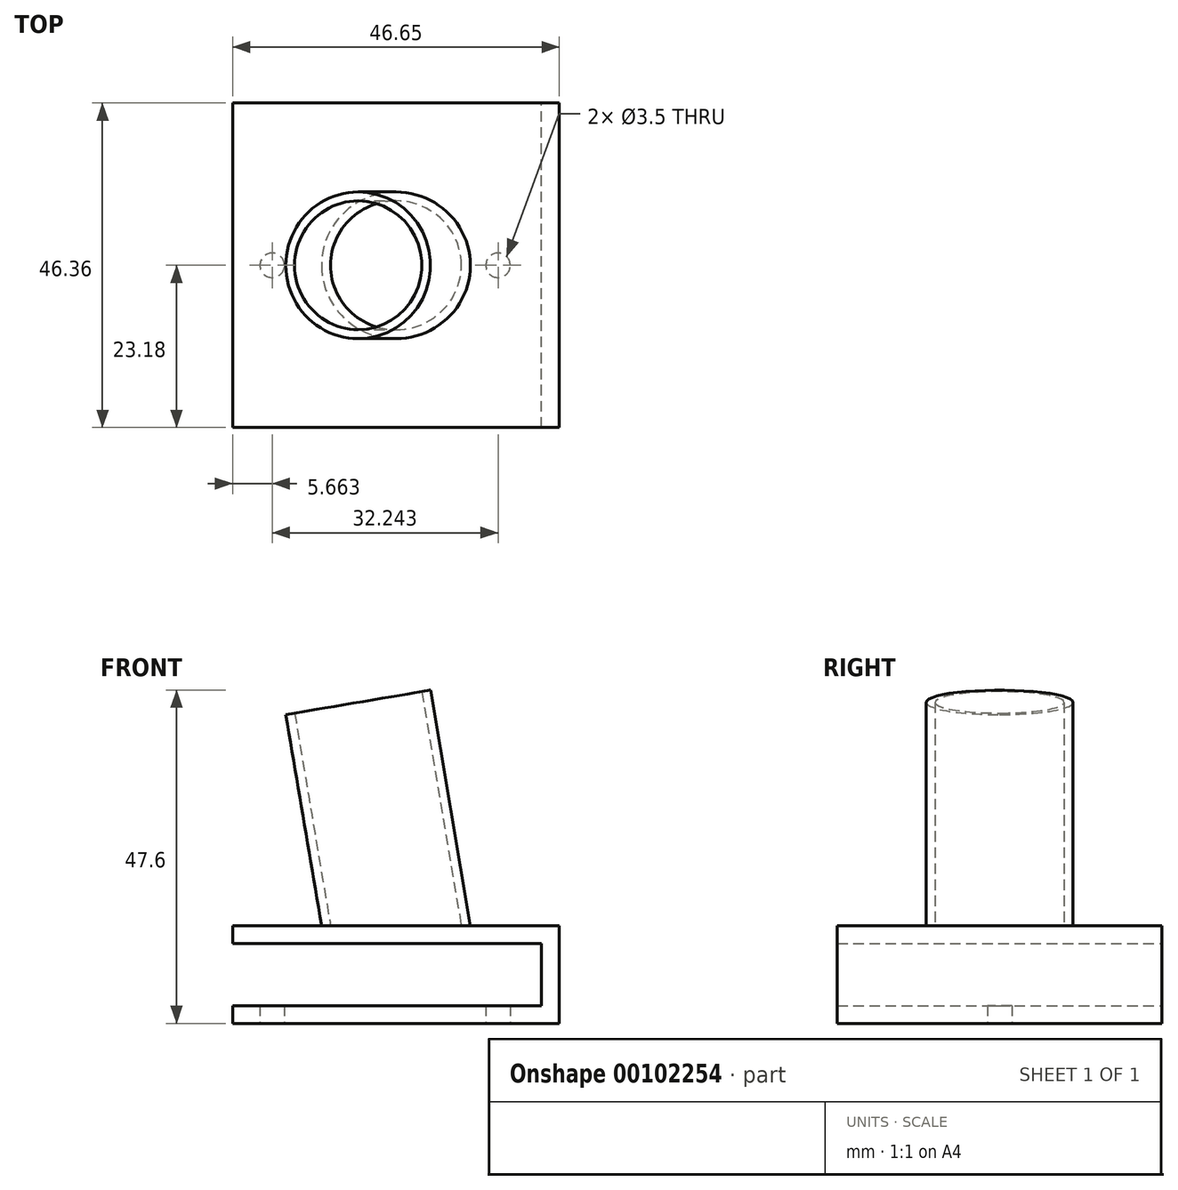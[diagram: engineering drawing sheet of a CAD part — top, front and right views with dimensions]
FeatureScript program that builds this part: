
annotation { "Feature Type Name" : "Feature", "Feature Type Description" : "" }
export const myFeature = defineFeature(function(context is Context, id is Id, definition is map)
    precondition{}
    {
        {
            var Q0;
            Q0=qCreatedBy(makeId("Top.planeOp"),FACE);
            var sketch = newSketch(context, id + "F0", { "sketchPlane" : qUnion([Q0])});
            skLineSegment(sketch, "E0", {"start": v(0, 75.88) * mm, "end": v(0, -75.68) * mm, "construction": true});
            skSolve(sketch);
        }
        {
            var Q0;
            Q0=sQuery(id+"F0.wireOp",EDGE,"E0");
            cPlane(context, id + "F1", {"entities" : qUnion([Q0]), "cplaneType" : CPlaneType.LINE_ANGLE, "offset" : 152.4 * mm, "angle" : 9.6 * degree, "width" : 152.4 * mm, "height" : 152.4 * mm});
        }
        {
            var Q0;
            Q0=qCreatedBy(id+"F1.planeOp",FACE);
            var sketch = newSketch(context, id + "F2", { "sketchPlane" : qUnion([Q0])});
            skCircle(sketch, "E1", {"center": v(41.03, 0) * mm, "radius": 9.2 * mm});
            skCircle(sketch, "E2", {"center": v(41.03, 0) * mm, "radius": 10.48 * mm});
            skSolve(sketch);
        }
        {
            var Q0;
            Q0 = qSketchRegion(id + "F2", true);
            extrude(context, id + "F3", {"entities" : qUnion([Q0]), "oppositeDirection" : true, "depth" : 25.4 * mm});
        }
        {
            var Q0;
            Q0=makeQuery(id+"F3.opExtrude","CAP_FACE",FACE,{"disambiguationData":[OSD([sQuery(id+"F2.wireOp",EDGE,"E1"),sQuery(id+"F2.wireOp",EDGE,"E2")])],"isStart":true});
            extrude(context, id + "F4", {"entities" : qUnion([Q0]), "operationType" : NewBodyOperationType.ADD, "depth" : 25.4 * mm});
        }
        {
            var Q0;
            Q0=qCreatedBy(makeId("Front.planeOp"),FACE);
            var sketch = newSketch(context, id + "F5", { "sketchPlane" : qUnion([Q0])});
            skLineSegment(sketch, "E3.bottom", {"start": v(59.9, 0) * mm, "end": v(18.37, 0) * mm});
            skLineSegment(sketch, "E3.top", {"start": v(59.9, -20.57) * mm, "end": v(18.37, -20.57) * mm});
            skLineSegment(sketch, "E3.left", {"start": v(59.9, 0) * mm, "end": v(59.9, -20.57) * mm});
            skLineSegment(sketch, "E3.right", {"start": v(18.37, 0) * mm, "end": v(18.37, -20.57) * mm});
            skSolve(sketch);
        }
        {
            var Q0;
            Q0 = qSketchRegion(id + "F5", true);
            extrude(context, id + "F6", {"entities" : qUnion([Q0]), "operationType" : NewBodyOperationType.REMOVE, "endBound" : BoundingType.SYMMETRIC, "oppositeDirection" : true, "depth" : 254 * mm});
        }
        {
            var Q0;
            Q0=qCreatedBy(makeId("Top.planeOp"),FACE);
            var sketch = newSketch(context, id + "F7", { "sketchPlane" : qUnion([Q0])});
            skLineSegment(sketch, "E4.bottom", {"start": v(18.29, 23.18) * mm, "end": v(64.94, 23.18) * mm});
            skLineSegment(sketch, "E4.top", {"start": v(18.29, -23.18) * mm, "end": v(64.94, -23.18) * mm});
            skLineSegment(sketch, "E4.left", {"start": v(18.29, 23.18) * mm, "end": v(18.29, -23.18) * mm});
            skLineSegment(sketch, "E4.right", {"start": v(64.94, 23.18) * mm, "end": v(64.94, -23.18) * mm});
            skLineSegment(sketch, "E5", {"start": v(52.24, 21.3) * mm, "end": v(52.24, -11.45) * mm, "construction": true});
            skLineSegment(sketch, "E6", {"start": v(23.5, -10.48) * mm, "end": v(51.74, -10.48) * mm, "construction": true});
            skLineSegment(sketch, "E7", {"start": v(30.99, -19.8) * mm, "end": v(30.99, 11.72) * mm, "construction": true});
            skSolve(sketch);
        }
        {
            var Q0;
            Q0=makeQuery(id+"F7.imprint","IMPRINT",FACE,{"disambiguationData":[TD([[makeQuery(id+"F7.imprint","IMPRINT",EDGE,{"derivedFrom":sQuery(id+"F7.wireOp",EDGE,"E4.bottom")}),-1.0]])]});
            extrude(context, id + "F8", {"entities" : qUnion([Q0]), "operationType" : NewBodyOperationType.ADD, "oppositeDirection" : true, "depth" : 2.54 * mm});
        }
        {
            var Q0;
            Q0=makeQuery(id+"F8.opExtrude","CAP_FACE",FACE,{"disambiguationData":[OSD([sQuery(id+"F7.wireOp",EDGE,"E4.bottom"),sQuery(id+"F7.wireOp",EDGE,"E4.top"),sQuery(id+"F7.wireOp",EDGE,"E4.left"),sQuery(id+"F7.wireOp",EDGE,"E4.right")])],"isStart":false});
            var sketch = newSketch(context, id + "F9", { "sketchPlane" : qUnion([Q0])});
            skLineSegment(sketch, "E8.bottom", {"start": v(62.4, 23.18) * mm, "end": v(64.94, 23.18) * mm});
            skLineSegment(sketch, "E8.top", {"start": v(62.4, -23.18) * mm, "end": v(64.94, -23.18) * mm});
            skLineSegment(sketch, "E8.left", {"start": v(62.4, 23.18) * mm, "end": v(62.4, -23.18) * mm});
            skLineSegment(sketch, "E8.right", {"start": v(64.94, 23.18) * mm, "end": v(64.94, -23.18) * mm});
            skSolve(sketch);
        }
        {
            var Q0;
            Q0 = qSketchRegion(id + "F9", true);
            extrude(context, id + "F10", {"entities" : qUnion([Q0]), "operationType" : NewBodyOperationType.ADD, "depth" : 8.9 * mm});
        }
        {
            var Q0;
            Q0=makeQuery(id+"F10.opExtrude","CAP_FACE",FACE,{"disambiguationData":[OSD([sQuery(id+"F9.wireOp",EDGE,"E8.bottom"),sQuery(id+"F9.wireOp",EDGE,"E8.top"),sQuery(id+"F9.wireOp",EDGE,"E8.left"),sQuery(id+"F9.wireOp",EDGE,"E8.right")])],"isStart":false});
            var sketch = newSketch(context, id + "F11", { "sketchPlane" : qUnion([Q0])});
            skLineSegment(sketch, "E9.bottom", {"start": v(64.94, 23.18) * mm, "end": v(18.29, 23.18) * mm});
            skLineSegment(sketch, "E9.top", {"start": v(64.94, -23.18) * mm, "end": v(18.29, -23.18) * mm});
            skLineSegment(sketch, "E9.left", {"start": v(64.94, 23.18) * mm, "end": v(64.94, -23.18) * mm});
            skLineSegment(sketch, "E9.right", {"start": v(18.29, 23.18) * mm, "end": v(18.29, -23.18) * mm});
            skSolve(sketch);
        }
        {
            var Q0;
            Q0 = qSketchRegion(id + "F11", true);
            extrude(context, id + "F12", {"entities" : qUnion([Q0]), "operationType" : NewBodyOperationType.ADD, "depth" : 2.54 * mm});
        }
        {
            var Q0;
            Q0=makeQuery(id+"F12.opExtrude","CAP_FACE",FACE,{"disambiguationData":[OSD([sQuery(id+"F11.wireOp",EDGE,"E9.bottom"),sQuery(id+"F11.wireOp",EDGE,"E9.top"),sQuery(id+"F11.wireOp",EDGE,"E9.left"),sQuery(id+"F11.wireOp",EDGE,"E9.right")])],"isStart":false});
            var sketch = newSketch(context, id + "F13", { "sketchPlane" : qUnion([Q0])});
            skCircle(sketch, "E10", {"center": v(23.95, 0) * mm, "radius": 1.75 * mm});
            skCircle(sketch, "E11", {"center": v(56.2, 0) * mm, "radius": 1.75 * mm});
            skSolve(sketch);
        }
        {
            var Q0;
            Q0 = qSketchRegion(id + "F13", true);
            extrude(context, id + "F14", {"entities" : qUnion([Q0]), "operationType" : NewBodyOperationType.REMOVE, "oppositeDirection" : true, "depth" : 2.54 * mm});
        }
    });
